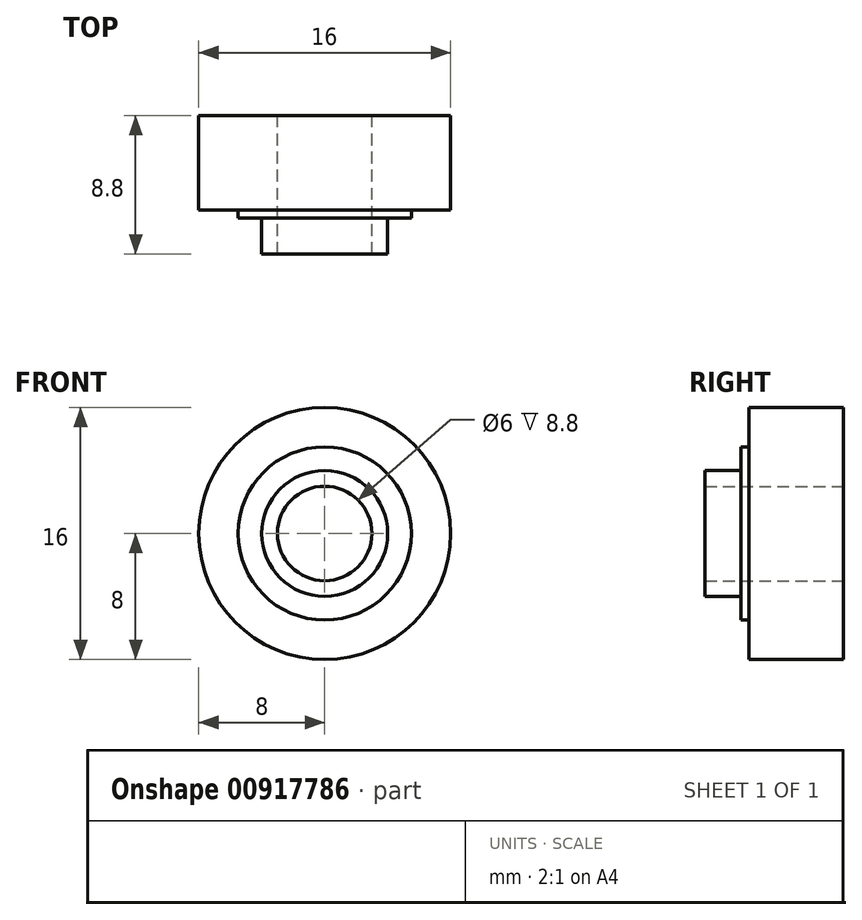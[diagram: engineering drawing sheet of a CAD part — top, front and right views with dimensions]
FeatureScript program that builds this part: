
annotation { "Feature Type Name" : "Feature", "Feature Type Description" : "" }
export const myFeature = defineFeature(function(context is Context, id is Id, definition is map)
    precondition{}
    {
        {
            var Q0;
            Q0=qCreatedBy(makeId("Front.planeOp"),FACE);
            var sketch = newSketch(context, id + "F0", { "sketchPlane" : qUnion([Q0])});
            skCircle(sketch, "E0", {"center": v(0, 0) * mm, "radius": 8 * mm});
            skSolve(sketch);
        }
        {
            var Q0;
            Q0=makeQuery(id+"F0.imprint","IMPRINT",FACE,{"disambiguationData":[TD([[makeQuery(id+"F0.imprint","IMPRINT",EDGE,{"derivedFrom":sQuery(id+"F0.wireOp",EDGE,"E0")}),1.0]])]});
            extrude(context, id + "F1", {"entities" : qUnion([Q0]), "depth" : 6 * mm, "offsetDistance" : 25.4 * mm});
        }
        {
            var Q0;
            Q0=makeQuery(id+"F1.opExtrude","CAP_FACE",FACE,{"disambiguationData":[OSD([sQuery(id+"F0.wireOp",EDGE,"E0")])],"isStart":false});
            var sketch = newSketch(context, id + "F2", { "sketchPlane" : qUnion([Q0])});
            skCircle(sketch, "E1", {"center": v(0, 0) * mm, "radius": 5.5 * mm});
            skSolve(sketch);
        }
        {
            var Q0;
            Q0=makeQuery(id+"F2.imprint","IMPRINT",FACE,{"disambiguationData":[TD([[makeQuery(id+"F2.imprint","IMPRINT",EDGE,{"derivedFrom":sQuery(id+"F2.wireOp",EDGE,"E1")}),1.0]])]});
            extrude(context, id + "F3", {"entities" : qUnion([Q0]), "operationType" : NewBodyOperationType.ADD, "depth" : .5 * mm, "offsetDistance" : 25.4 * mm});
        }
        {
            var Q0;
            Q0=makeQuery(id+"F3.opExtrude","CAP_FACE",FACE,{"disambiguationData":[OSD([sQuery(id+"F2.wireOp",EDGE,"E1")])],"isStart":false});
            var sketch = newSketch(context, id + "F4", { "sketchPlane" : qUnion([Q0])});
            skCircle(sketch, "E2", {"center": v(0, 0) * mm, "radius": 4 * mm});
            skCircle(sketch, "E3", {"center": v(0, 0) * mm, "radius": 3 * mm});
            skSolve(sketch);
        }
        {
            var Q0;
            Q0=makeQuery(id+"F4.imprint","IMPRINT",FACE,{"disambiguationData":[TD([[makeQuery(id+"F4.imprint","IMPRINT",EDGE,{"derivedFrom":sQuery(id+"F4.wireOp",EDGE,"E2")}),1.0]])]});
            extrude(context, id + "F5", {"entities" : qUnion([Q0]), "operationType" : NewBodyOperationType.ADD, "depth" : 2.3 * mm, "offsetDistance" : 25.4 * mm});
        }
        {
            var Q0;
            Q0=makeQuery(id+"F5.boolean.opBoolean","SPLIT",FACE,{"disambiguationData":[TD([makeQuery(id+"F5.opExtrude","SWEPT_FACE",FACE,{"disambiguationData":[OSD([sQuery(id+"F4.wireOp",EDGE,"E3")])]})])],"derivedFrom":makeQuery(id+"F3.opExtrude","CAP_FACE",FACE,{"disambiguationData":[OSD([sQuery(id+"F2.wireOp",EDGE,"E1")])],"isStart":false})});
            extrude(context, id + "F6", {"entities" : qUnion([Q0]), "operationType" : NewBodyOperationType.REMOVE, "endBound" : BoundingType.THROUGH_ALL, "oppositeDirection" : true, "depth" : 25.4 * mm, "offsetDistance" : 25.4 * mm});
        }
    });
